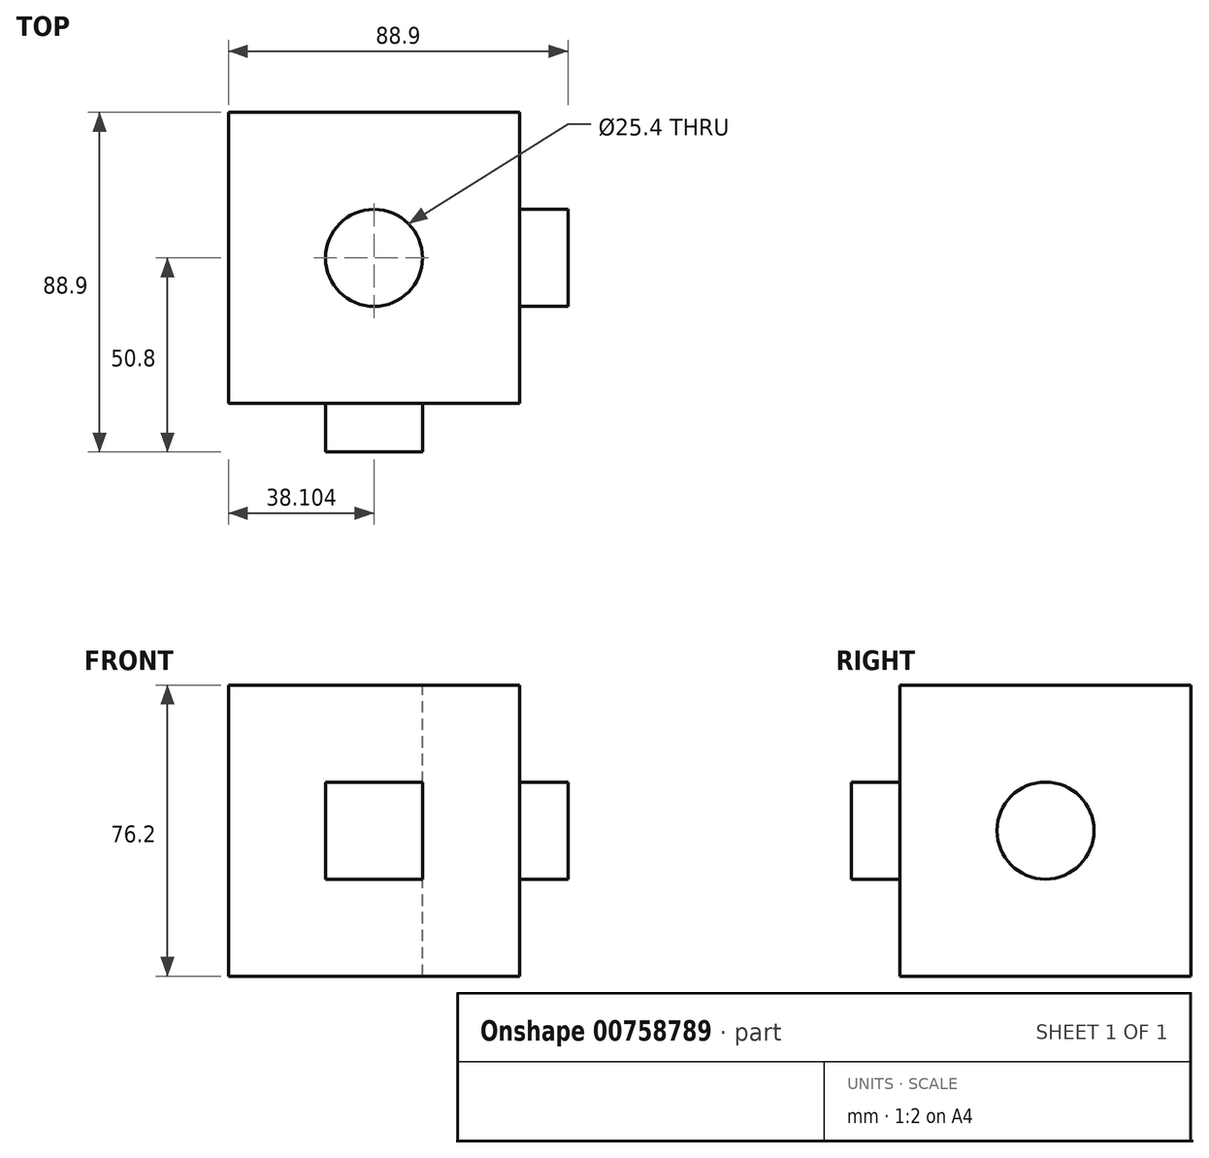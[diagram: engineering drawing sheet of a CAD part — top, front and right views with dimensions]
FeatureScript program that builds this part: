
annotation { "Feature Type Name" : "Feature", "Feature Type Description" : "" }
export const myFeature = defineFeature(function(context is Context, id is Id, definition is map)
    precondition{}
    {
        {
            var Q0;
            Q0=qCreatedBy(makeId("Front.planeOp"),FACE);
            var sketch = newSketch(context, id + "F0", { "sketchPlane" : qUnion([Q0])});
            skLineSegment(sketch, "E0.bottom", {"start": v(-58.96, 22.82) * mm, "end": v(17.24, 22.82) * mm});
            skLineSegment(sketch, "E0.top", {"start": v(-58.96, -53.38) * mm, "end": v(17.24, -53.38) * mm});
            skLineSegment(sketch, "E0.left", {"start": v(-58.96, 22.82) * mm, "end": v(-58.96, -53.38) * mm});
            skLineSegment(sketch, "E0.right", {"start": v(17.24, 22.82) * mm, "end": v(17.24, -53.38) * mm});
            skSolve(sketch);
        }
        {
            var Q0;
            Q0=makeQuery(id+"F0.imprint","IMPRINT",FACE,{"disambiguationData":[TD([[makeQuery(id+"F0.imprint","IMPRINT",EDGE,{"derivedFrom":sQuery(id+"F0.wireOp",EDGE,"E0.bottom")}),-1.0]])]});
            extrude(context, id + "F1", {"entities" : qUnion([Q0]), "depth" : 76.2 * mm, "offsetDistance" : 25.4 * mm});
        }
        {
            var Q0;
            Q0=makeQuery(id+"F1.opExtrude","CAP_FACE",FACE,{"disambiguationData":[OSD([sQuery(id+"F0.wireOp",EDGE,"E0.bottom"),sQuery(id+"F0.wireOp",EDGE,"E0.top"),sQuery(id+"F0.wireOp",EDGE,"E0.left"),sQuery(id+"F0.wireOp",EDGE,"E0.right")])],"isStart":false});
            var sketch = newSketch(context, id + "F2", { "sketchPlane" : qUnion([Q0])});
            skLineSegment(sketch, "E1.bottom", {"start": v(-33.56, -2.58) * mm, "end": v(-8.16, -2.58) * mm});
            skLineSegment(sketch, "E1.top", {"start": v(-33.56, -27.98) * mm, "end": v(-8.16, -27.98) * mm});
            skLineSegment(sketch, "E1.left", {"start": v(-33.56, -2.58) * mm, "end": v(-33.56, -27.98) * mm});
            skLineSegment(sketch, "E1.right", {"start": v(-8.16, -2.58) * mm, "end": v(-8.16, -27.98) * mm});
            skSolve(sketch);
        }
        {
            var Q0;
            Q0=makeQuery(id+"F2.imprint","IMPRINT",FACE,{"disambiguationData":[TD([[makeQuery(id+"F2.imprint","IMPRINT",EDGE,{"derivedFrom":sQuery(id+"F2.wireOp",EDGE,"E1.bottom")}),-1.0]])]});
            extrude(context, id + "F3", {"entities" : qUnion([Q0]), "operationType" : NewBodyOperationType.ADD, "depth" : 12.7 * mm, "offsetDistance" : 25.4 * mm});
        }
        {
            var Q0;
            Q0=makeQuery(id+"F1.opExtrude","SWEPT_FACE",FACE,{"disambiguationData":[OSD([sQuery(id+"F0.wireOp",EDGE,"E0.right")])]});
            var sketch = newSketch(context, id + "F4", { "sketchPlane" : qUnion([Q0])});
            skCircle(sketch, "E2", {"center": v(-38.1, -15.28) * mm, "radius": 12.7 * mm});
            skSolve(sketch);
        }
        {
            var Q0;
            Q0=makeQuery(id+"F4.imprint","IMPRINT",FACE,{"disambiguationData":[TD([[makeQuery(id+"F4.imprint","IMPRINT",EDGE,{"derivedFrom":sQuery(id+"F4.wireOp",EDGE,"E2")}),1.0]])]});
            extrude(context, id + "F5", {"entities" : qUnion([Q0]), "operationType" : NewBodyOperationType.ADD, "depth" : 12.7 * mm, "offsetDistance" : 25.4 * mm});
        }
        {
            var Q0;
            Q0=makeQuery(id+"F1.opExtrude","SWEPT_FACE",FACE,{"disambiguationData":[OSD([sQuery(id+"F0.wireOp",EDGE,"E0.bottom")])]});
            var sketch = newSketch(context, id + "F6", { "sketchPlane" : qUnion([Q0])});
            skPoint(sketch, "E3", {"position": v(-20.86, -38.1) * mm});
            skPoint(sketch, "E3.positionSnap0", {"position": v(-58.96, -38.1) * mm});
            skSolve(sketch);
        }
        {
            var Q0;
            Q0=sQuery(id+"F6.wireOp",VERTEX,"E3");
            var Q1;
            Q1=makeQuery(id+"F1.opExtrude","SWEPT_BODY",BODY,{"disambiguationData":[OSD([sQuery(id+"F0.wireOp",EDGE,"E0.bottom"),sQuery(id+"F0.wireOp",EDGE,"E0.top"),sQuery(id+"F0.wireOp",EDGE,"E0.left"),sQuery(id+"F0.wireOp",EDGE,"E0.right")])]});
            hole(context, id + "F7", {"style" : HoleStyle.SIMPLE, "endStyle" : HoleEndStyle.THROUGH, "holeDiameter" : 25.4 * mm, "majorDiameter" : 6.35 * mm, "isTappedThrough" : true, "tappedDepth" : 12.7 * mm, "tapClearance" : 3, "locations" : qUnion([Q0]), "scope" : qUnion([Q1])});
        }
    });
